# Revit family: JC KONTAKTER JCK119 DE
name_source: partatom
category: Specialty Equipment
units: mm (PartAtom-declared; Revit-internal decimal feet)

## family parameters
Cut with Voids When Loaded = No
Enable Cutting in Views = Yes
Host = Face
Maintain Annotation Orientation = Yes
Part Type = Normal
Room Calculation Point = No
Round Connector Dimension = Use Diameter
Shared = No

## types (1)
- JCK119
    Anzahl der mikroschalter = 2
    CE-kennzeichnung = https://jckontakter.se
    Deckel = Messing
    Default Elevation = 800 mm  [stored 2.62467 ft]
    Description = JCK119 ist ein robuster Großflächentaster mit flacher Druckplatte und Endkappe aus Messing sowie einem Unterteil aus goldeloxiertem Aluminium. Das Modell wurde für den Einsatz in exklusiven Umgebungen und denkmalgeschützten Gebäuden entwickelt. JCK119 kann auch mit Funksteuerung bestellt werden, da es in älteren Gebäuden oft schwierig ist, Kabel zu verlegen.
    Endkappen = Messing
    Geringster nennstrom = 1mA/4 V DC
    Herstellungsland = Schweden
    Kern = Aluminum ENAW 6060-T6 (goldeloxiert)
    Manufacturer = JC kontakter
    Mikroschalter = Standard NO IP67
    Model = JCK119
    Nomineller nennstrom = 12 V - Resistive 6A Inductive L/R 5ms 6A, 24 V - Resistive 6A Inductive L/R 5ms 5A
    Produktgewicht = 0.619 kg.
    Technisches Produktblatt = https://grossflaechentaster.de
    URL = https://grossflaechentaster.de

note: [stored X ft] marks values corroborated as IEEE doubles in the binary element streams (Revit-internal decimal feet)

## geometry (parser evidence)
native form markers: Sweep x6
no freeform markers — native parametric forms only
